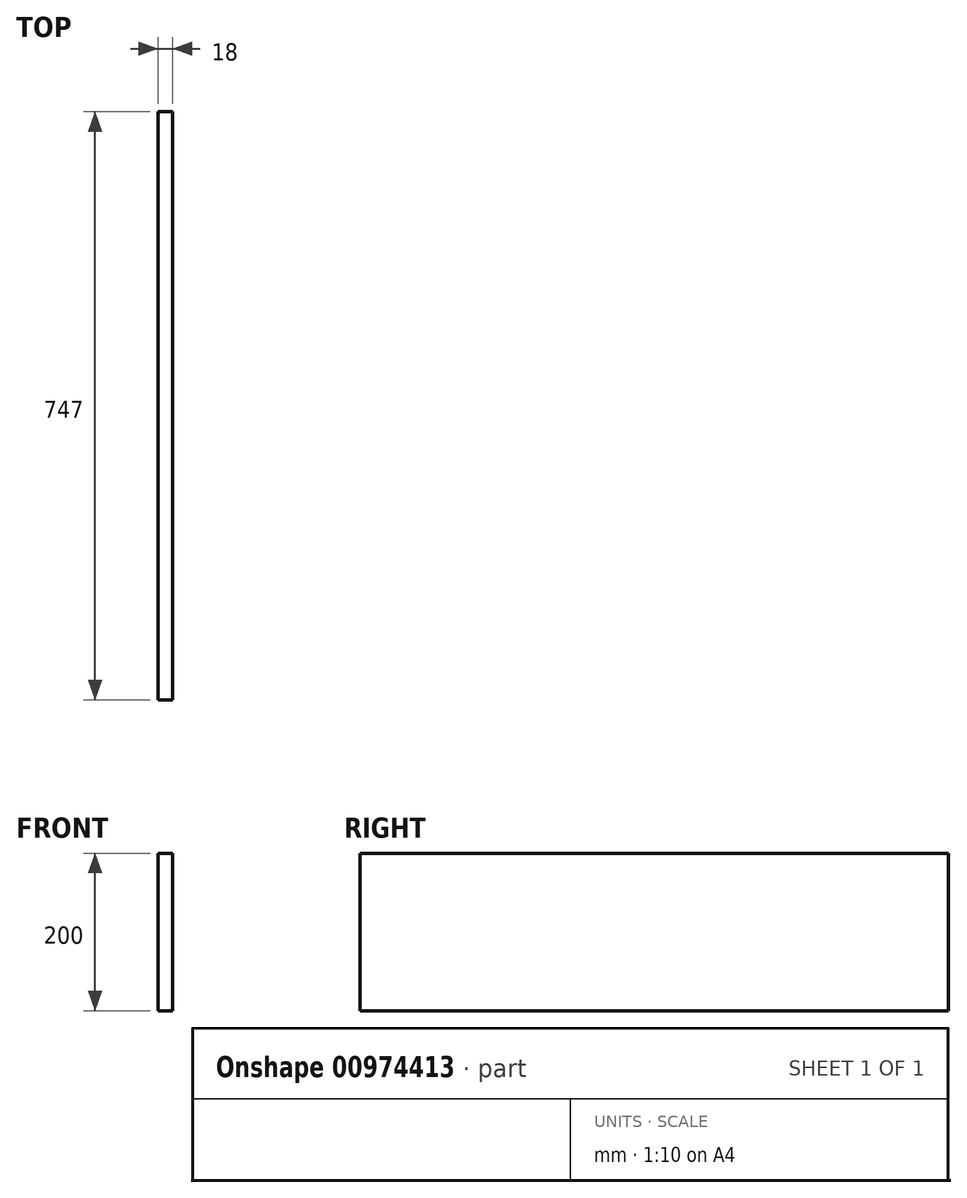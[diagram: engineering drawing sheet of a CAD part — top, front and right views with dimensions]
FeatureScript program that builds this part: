
annotation { "Feature Type Name" : "Feature", "Feature Type Description" : "" }
export const myFeature = defineFeature(function(context is Context, id is Id, definition is map)
    precondition{}
    {
        {
            var Q0;
            Q0=qCreatedBy(makeId("Right.planeOp"),FACE);
            var sketch = newSketch(context, id + "F0", { "sketchPlane" : qUnion([Q0])});
            skLineSegment(sketch, "E0.bottom", {"start": v(373.5, 100) * mm, "end": v(-373.5, 100) * mm});
            skLineSegment(sketch, "E0.top", {"start": v(373.5, -100) * mm, "end": v(-373.5, -100) * mm});
            skLineSegment(sketch, "E0.left", {"start": v(373.5, 100) * mm, "end": v(373.5, -100) * mm});
            skLineSegment(sketch, "E0.right", {"start": v(-373.5, 100) * mm, "end": v(-373.5, -100) * mm});
            skPoint(sketch, "E0.middle", {"position": v(0, 0) * mm});
            skSolve(sketch);
        }
        {
            var Q0;
            Q0=makeQuery(id+"F0.imprint","IMPRINT",FACE,{"disambiguationData":[TD([[makeQuery(id+"F0.imprint","IMPRINT",EDGE,{"derivedFrom":sQuery(id+"F0.wireOp",EDGE,"E0.bottom")}),1.0]])]});
            extrude(context, id + "F1", {"entities" : qUnion([Q0]), "depth" : 18 * mm, "offsetDistance" : 25 * mm});
        }
    });
